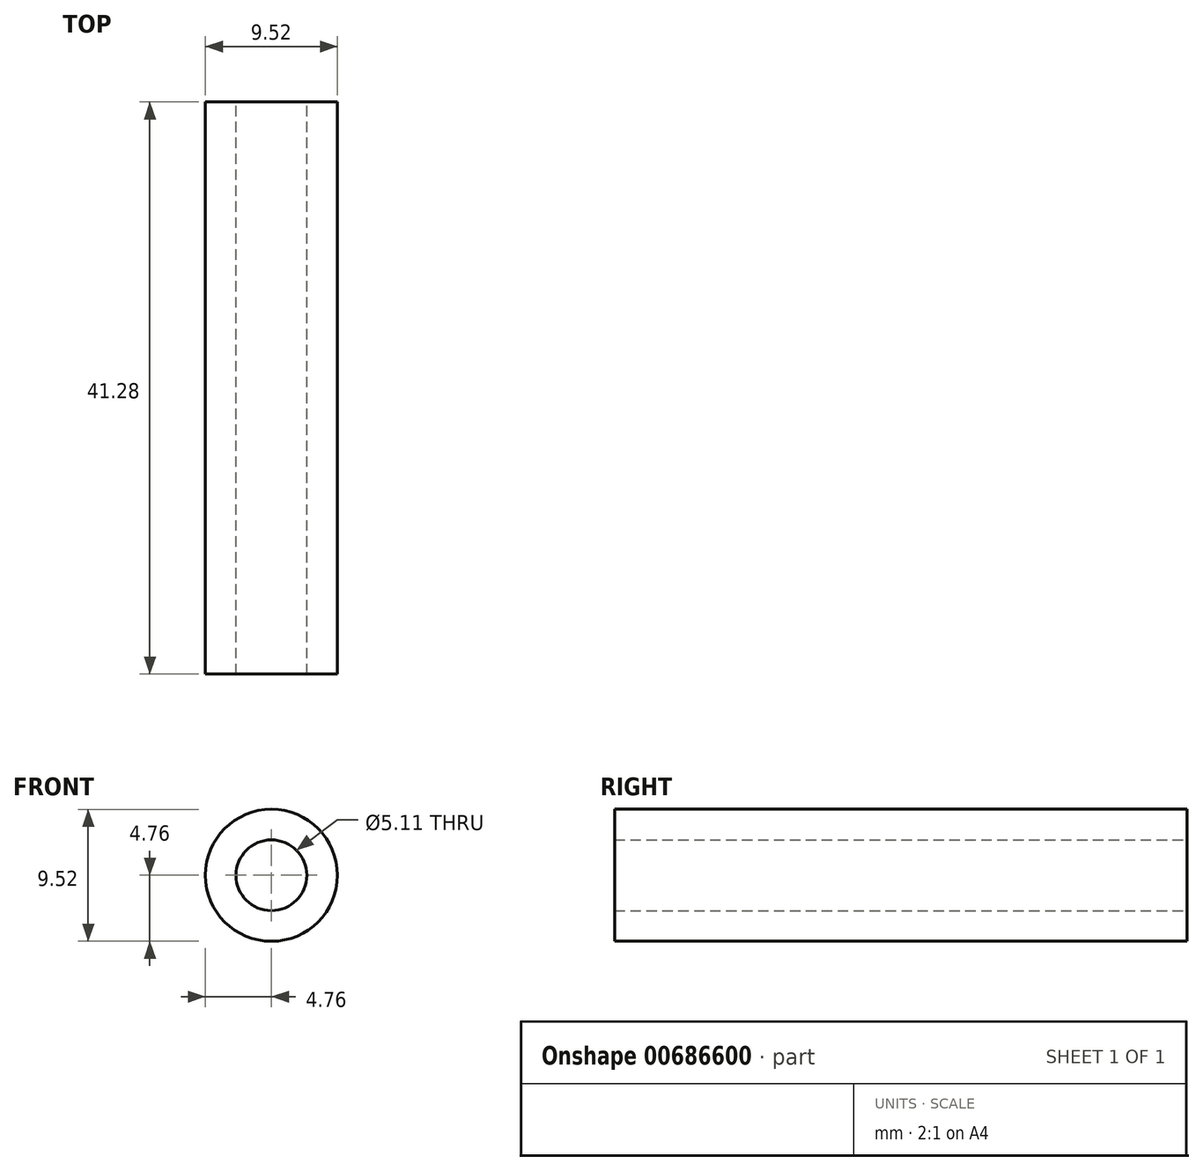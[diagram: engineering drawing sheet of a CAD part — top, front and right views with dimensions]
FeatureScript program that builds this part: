
annotation { "Feature Type Name" : "Feature", "Feature Type Description" : "" }
export const myFeature = defineFeature(function(context is Context, id is Id, definition is map)
    precondition{}
    {
        {
            var Q0;
            Q0=qCreatedBy(makeId("Front.planeOp"),FACE);
            var sketch = newSketch(context, id + "F0", { "sketchPlane" : qUnion([Q0])});
            skCircle(sketch, "E0", {"center": v(0, 0) * mm, "radius": 2.55 * mm});
            skCircle(sketch, "E1", {"center": v(0, 0) * mm, "radius": 4.76 * mm});
            skSolve(sketch);
        }
        {
            var Q0;
            Q0 = qSketchRegion(id + "F0", true);
            extrude(context, id + "F1", {"entities" : qUnion([Q0]), "endBound" : BoundingType.SYMMETRIC, "depth" : 41.27 * mm, "offsetDistance" : 25.4 * mm});
        }
    });
